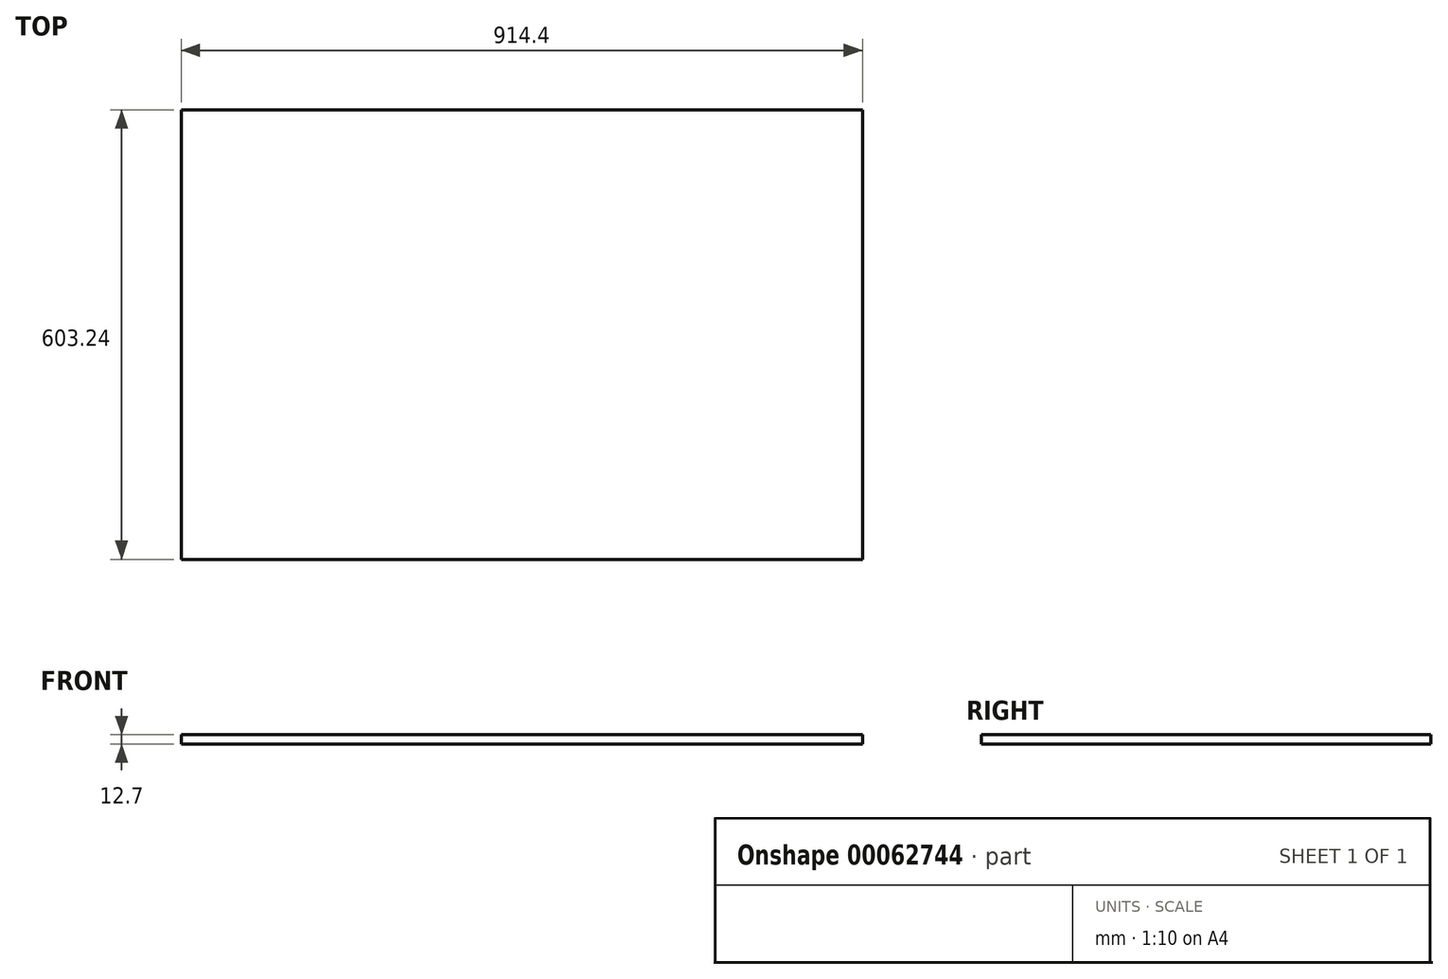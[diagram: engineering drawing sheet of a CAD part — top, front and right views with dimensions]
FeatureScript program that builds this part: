
annotation { "Feature Type Name" : "Feature", "Feature Type Description" : "" }
export const myFeature = defineFeature(function(context is Context, id is Id, definition is map)
    precondition{}
    {
        {
            var Q0;
            Q0=qCreatedBy(makeId("Top.planeOp"),FACE);
            var sketch = newSketch(context, id + "F0", { "sketchPlane" : qUnion([Q0])});
            skLineSegment(sketch, "E0.rect.bottom", {"start": v(457.2, -301.62) * mm, "end": v(-457.2, -301.63) * mm});
            skLineSegment(sketch, "E0.rect.top", {"start": v(457.2, 301.63) * mm, "end": v(-457.2, 301.62) * mm});
            skLineSegment(sketch, "E0.rect.left", {"start": v(457.2, -301.62) * mm, "end": v(457.2, 301.63) * mm});
            skLineSegment(sketch, "E0.rect.right", {"start": v(-457.2, -301.63) * mm, "end": v(-457.2, 301.62) * mm});
            skPoint(sketch, "E0.rect.middle", {"position": v(0, 0) * mm});
            skSolve(sketch);
        }
        {
            var Q0;
            Q0 = qSketchRegion(id + "F0", true);
            extrude(context, id + "F1", {"entities" : qUnion([Q0]), "depth" : 12.7 * mm});
        }
        {
            var Q0;
            Q0=makeQuery(id+"F1.opExtrude","CAP_FACE",FACE,{"disambiguationData":[OSD([sQuery(id+"F0.wireOp",EDGE,"E0.rect.bottom"),sQuery(id+"F0.wireOp",EDGE,"E0.rect.top"),sQuery(id+"F0.wireOp",EDGE,"E0.rect.left"),sQuery(id+"F0.wireOp",EDGE,"E0.rect.right")])],"isStart":false});
            var sketch = newSketch(context, id + "F2", { "sketchPlane" : qUnion([Q0])});
            skPoint(sketch, "E1", {"position": v(-447.04, -291.47) * mm});
            skPoint(sketch, "E2", {"position": v(-447.04, 145.41) * mm});
            skPoint(sketch, "E3", {"position": v(300.99, -149.22) * mm});
            skPoint(sketch, "E4", {"position": v(300.99, 145.41) * mm});
            skSolve(sketch);
        }
    });
